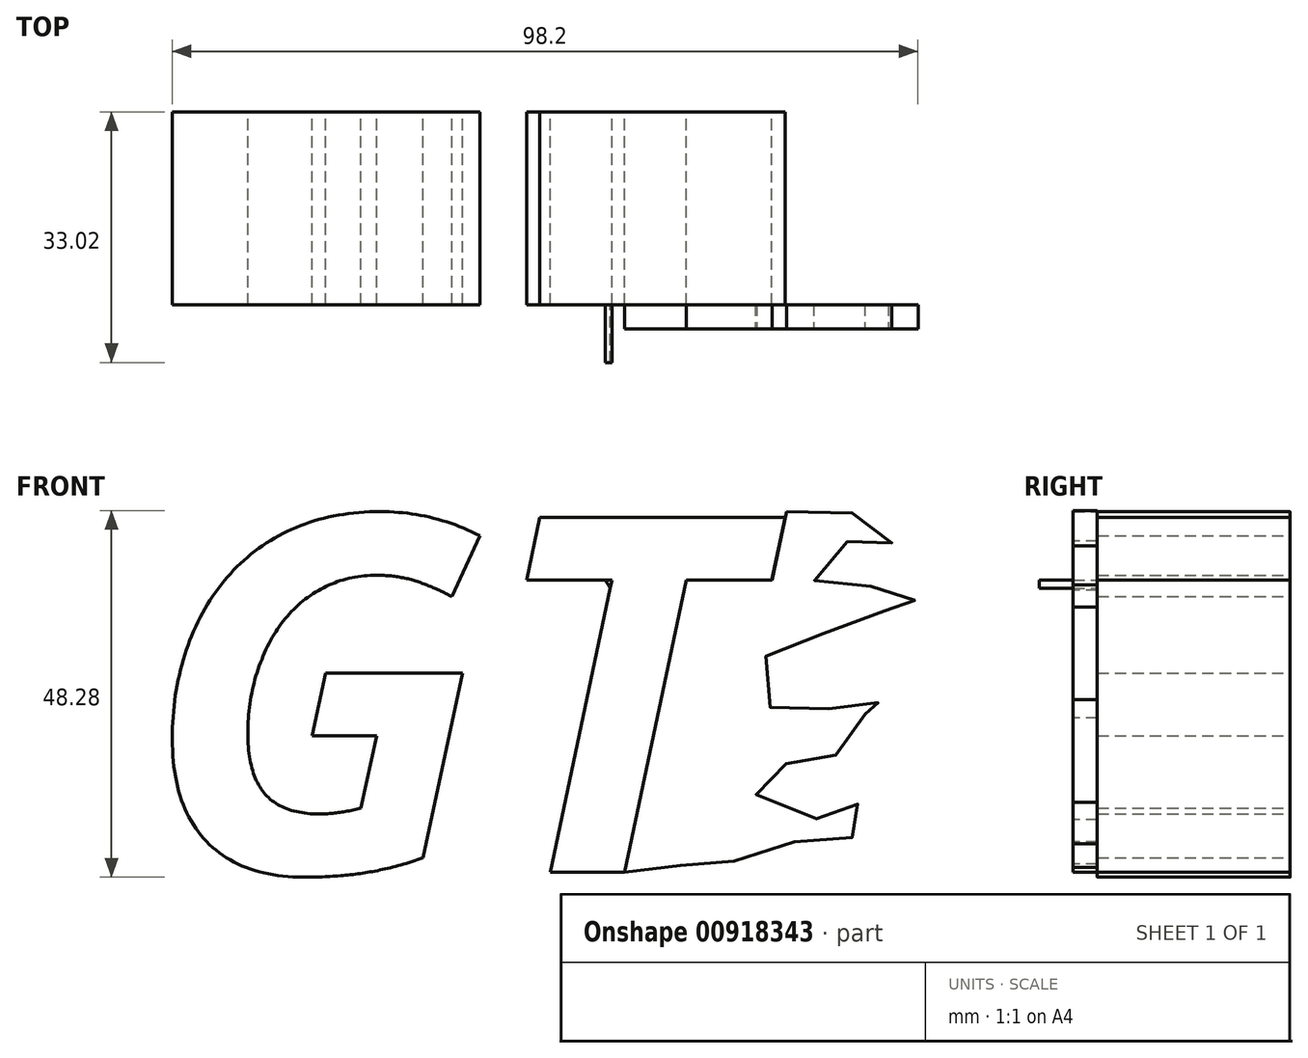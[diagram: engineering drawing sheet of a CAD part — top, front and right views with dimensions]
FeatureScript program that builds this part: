
annotation { "Feature Type Name" : "Feature", "Feature Type Description" : "" }
export const myFeature = defineFeature(function(context is Context, id is Id, definition is map)
    precondition{}
    {
        {
            var Q0;
            Q0=qCreatedBy(makeId("Front.planeOp"),FACE);
            var sketch = newSketch(context, id + "F0", { "sketchPlane" : qUnion([Q0])});
            skText(sketch, "E0", { "text": "GT", "fontName": "NotoSans-BoldItalic.ttf"});
            const initialGuessF0  = {"E0": [-0.04445, -0.02032, 1, 0, 0.04717]};
            skSetInitialGuess(sketch, initialGuessF0);
            skSolve(sketch);
        }
        {
            var Q0;
            Q0 = qSketchRegion(id + "F0", true);
            extrude(context, id + "F1", {"entities" : qUnion([Q0]), "depth" : 25.4 * mm, "offsetDistance" : 25.4 * mm});
        }
        {
            var Q0;
            Q0=makeQuery(id+"F1.opExtrude","CAP_FACE",FACE,{"disambiguationData":[OSD([sQuery(id+"F0.wireOp",EDGE,"E0.sketch_text.stroke-0"),sQuery(id+"F0.wireOp",EDGE,"E0.sketch_text.stroke-1"),sQuery(id+"F0.wireOp",EDGE,"E0.sketch_text.stroke-2"),sQuery(id+"F0.wireOp",EDGE,"E0.sketch_text.stroke-3"),sQuery(id+"F0.wireOp",EDGE,"E0.sketch_text.stroke-4"),sQuery(id+"F0.wireOp",EDGE,"E0.sketch_text.stroke-5"),sQuery(id+"F0.wireOp",EDGE,"E0.sketch_text.stroke-6"),sQuery(id+"F0.wireOp",EDGE,"E0.sketch_text.stroke-7"),sQuery(id+"F0.wireOp",EDGE,"E0.sketch_text.stroke-8"),sQuery(id+"F0.wireOp",EDGE,"E0.sketch_text.stroke-9"),sQuery(id+"F0.wireOp",EDGE,"E0.sketch_text.stroke-10"),sQuery(id+"F0.wireOp",EDGE,"E0.sketch_text.stroke-11"),sQuery(id+"F0.wireOp",EDGE,"E0.sketch_text.stroke-12"),sQuery(id+"F0.wireOp",EDGE,"E0.sketch_text.stroke-13"),sQuery(id+"F0.wireOp",EDGE,"E0.sketch_text.stroke-14"),sQuery(id+"F0.wireOp",EDGE,"E0.sketch_text.stroke-15"),sQuery(id+"F0.wireOp",EDGE,"E0.sketch_text.stroke-16"),sQuery(id+"F0.wireOp",EDGE,"E0.sketch_text.stroke-17"),sQuery(id+"F0.wireOp",EDGE,"E0.sketch_text.stroke-18"),sQuery(id+"F0.wireOp",EDGE,"E0.sketch_text.stroke-19"),sQuery(id+"F0.wireOp",EDGE,"E0.sketch_text.stroke-20"),sQuery(id+"F0.wireOp",EDGE,"E0.sketch_text.stroke-21")])],"isStart":false});
            cPlane(context, id + "F2", {"entities" : qUnion([Q0]), "cplaneType" : CPlaneType.OFFSET, "offset" : 0 * mm, "width" : 152.4 * mm, "height" : 152.4 * mm});
        }
        {
            var Q0;
            Q0=qCreatedBy(id+"F2.planeOp",FACE);
            var sketch = newSketch(context, id + "F3", { "sketchPlane" : qUnion([Q0])});
            skFitSpline(sketch, "E1.0", {"points": [v(-37.14, 12.66) * mm, v(-33.76, 19.57) * mm, v(-27.59, 23.38) * mm]});
            skFitSpline(sketch, "E1.1", {"points": [v(-27.59, 23.38) * mm, v(-21.42, 27.19) * mm, v(-13.13, 27.19) * mm]});
            skFitSpline(sketch, "E1.6", {"points": [v(-13.57, 18.8) * mm, v(-18.47, 18.8) * mm, v(-22.33, 16.15) * mm]});
            skFitSpline(sketch, "E1.7", {"points": [v(-22.33, 16.15) * mm, v(-26.19, 13.5) * mm, v(-28.38, 8.58) * mm]});
            skFitSpline(sketch, "E1.8", {"points": [v(-28.38, 8.58) * mm, v(-30.57, 3.67) * mm, v(-30.57, -1.99) * mm]});
            skFitSpline(sketch, "E1.9", {"points": [v(-30.57, -1.99) * mm, v(-30.57, -7.5) * mm, v(-28.25, -10.07) * mm]});
            skFitSpline(sketch, "E1.10", {"points": [v(-28.25, -10.07) * mm, v(-25.93, -12.65) * mm, v(-21.13, -12.65) * mm]});
            skFitSpline(sketch, "E1.11", {"points": [v(-21.13, -12.65) * mm, v(-18.7, -12.65) * mm, v(-15.7, -11.88) * mm]});
            skLineSegment(sketch, "E1.12", {"start": v(-15.16, -9.47) * mm, "end": v(-13.57, -2.32) * mm});
            skLineSegment(sketch, "E1.13", {"start": v(-13.57, -2.32) * mm, "end": v(-22.12, -2.32) * mm});
            skLineSegment(sketch, "E1.14", {"start": v(-22.12, -2.32) * mm, "end": v(-20.33, 5.95) * mm});
            skLineSegment(sketch, "E1.15", {"start": v(-20.33, 5.95) * mm, "end": v(-2.31, 5.95) * mm});
            skLineSegment(sketch, "E1.16", {"start": v(-2.31, 5.95) * mm, "end": v(-6.89, -15.53) * mm});
            skFitSpline(sketch, "E1.17", {"points": [v(-7.5, -18.44) * mm, v(-11.78, -19.9) * mm, v(-15.45, -20.44) * mm]});
            skFitSpline(sketch, "E1.18", {"points": [v(-15.45, -20.44) * mm, v(-19.11, -20.97) * mm, v(-23.2, -20.97) * mm]});
            skFitSpline(sketch, "E1.19", {"points": [v(-23.2, -20.97) * mm, v(-31.49, -20.97) * mm, v(-36, -16.26) * mm]});
            skFitSpline(sketch, "E1.20", {"points": [v(-36, -16.26) * mm, v(-40.52, -11.56) * mm, v(-40.52, -2.76) * mm]});
            skFitSpline(sketch, "E1.21", {"points": [v(-40.52, -2.76) * mm, v(-40.52, 5.75) * mm, v(-37.14, 12.66) * mm]});
            skLineSegment(sketch, "E2.2", {"start": v(40.2, 26.45) * mm, "end": v(38.44, 18.2) * mm});
            skLineSegment(sketch, "E2.3", {"start": v(38.44, 18.2) * mm, "end": v(27.15, 18.2) * mm});
            skLineSegment(sketch, "E2.4", {"start": v(27.15, 18.2) * mm, "end": v(19.02, -20.32) * mm});
            skLineSegment(sketch, "E2.5", {"start": v(19.02, -20.32) * mm, "end": v(9.26, -20.32) * mm});
            skLineSegment(sketch, "E2.6", {"start": v(9.26, -20.32) * mm, "end": v(17.4, 18.2) * mm});
            skLineSegment(sketch, "E2.7", {"start": v(17.4, 18.2) * mm, "end": v(6.13, 18.2) * mm});
            skLineSegment(sketch, "E3", {"start": v(-13.13, 27.19) * mm, "end": v(40.36, 27.19) * mm});
            skLineSegment(sketch, "E4", {"start": v(6.13, 18.2) * mm, "end": v(-16.98, 18.2) * mm});
            skPoint(sketch, "E5.orphan", {"position": v(-3.7, 15.99) * mm});
            skPoint(sketch, "E6.orphan", {"position": v(-8.43, 18.04) * mm});
            skPoint(sketch, "E7.orphan", {"position": v(-13.57, 18.8) * mm});
            skPoint(sketch, "E1.2.end.orphan", {"position": v(-0.01, 24.01) * mm});
            skPoint(sketch, "E2.1.start.orphan", {"position": v(7.9, 26.45) * mm});
            skLineSegment(sketch, "E8", {"start": v(40.2, 26.45) * mm, "end": v(40.36, 27.19) * mm});
            skPoint(sketch, "E9.visualSharp", {"position": v(-18, 18.2) * mm});
            skArc(sketch, "E9.filletArc", {"start": v(-16.98, 18.2) * mm, "mid": v(-18.16, 18.09) * mm, "end": v(-19.3, 17.76) * mm});
            skPoint(sketch, "E10.visualSharp", {"position": v(-15.7, -11.88) * mm});
            skArc(sketch, "E10.filletArc", {"start": v(-18.3, -12.42) * mm, "mid": v(-16.28, -11.43) * mm, "end": v(-15.16, -9.47) * mm});
            skPoint(sketch, "E11.visualSharp", {"position": v(-7.5, -18.44) * mm});
            skArc(sketch, "E11.filletArc", {"start": v(-10.5, -19.37) * mm, "mid": v(-8.15, -17.95) * mm, "end": v(-6.89, -15.53) * mm});
            skArc(sketch, "E12", {"start": v(-14.72, 33.34) * mm, "mid": v(-45.06, -1.74) * mm, "end": v(-11.23, -33.48) * mm, "construction": true});
            skFitSpline(sketch, "E13", {"points": [v(-14.72, 33.34) * mm, v(37.18, 33.37) * mm, v(58.87, 35.5) * mm, v(76.74, 32.31) * mm, v(64.4, 31.46) * mm, v(56.96, 24.65) * mm, v(67.5, 20.64) * mm, v(87.92, 28.3) * mm, v(67.08, 12.56) * mm, v(53.46, 11.07) * mm, v(61.33, 0) * mm, v(87.92, 10.86) * mm, v(69.63, -7.22) * mm, v(52.19, -9.99) * mm, v(62.82, -20.2) * mm, v(80.48, -9.35) * mm, v(64.31, -28.07) * mm, v(-11.23, -33.48) * mm], "startDerivative": vector(608.28, -20.2) * mm, "endDerivative": vector(-707.93, -8.2) * mm, "construction": true});
            skArc(sketch, "E14.trimOffspring", {"start": v(17.16, 17.1) * mm, "mid": v(16.83, 17.66) * mm, "end": v(16.49, 18.2) * mm});
            skFitSpline(sketch, "E15", {"points": [v(40.36, 27.19) * mm, v(47.88, 27.19) * mm, v(52.24, 25.58) * mm, v(54.2, 22.87) * mm, v(50.74, 23.17) * mm, v(46.83, 22.57) * mm, v(43.97, 18.36) * mm, v(47.28, 16.86) * mm, v(54.2, 17.46) * mm, v(56.76, 15.95) * mm, v(57.66, 14.75) * mm, v(54.65, 14.6) * mm, v(50.14, 12.35) * mm, v(41.42, 10.4) * mm, v(37.35, 7.68) * mm, v(36.9, 2.87) * mm, v(42.62, 0) * mm, v(47.28, 1.97) * mm, v(51.34, 2.27) * mm, v(53.75, 1.52) * mm, v(51.8, 1.22) * mm, v(49.69, -1.2) * mm, v(46.98, -4.8) * mm, v(43.07, -5.55) * mm, v(38.86, -6.6) * mm, v(36.3, -9.16) * mm, v(37.8, -11.57) * mm, v(46.38, -13.37) * mm, v(48.63, -12.47) * mm, v(50.29, -11.12) * mm, v(50.29, -14.27) * mm, v(46.53, -16.53) * mm, v(40.36, -16.38) * mm, v(34.05, -18.64) * mm, v(28.63, -19.69) * mm, v(24.72, -19.24) * mm, v(19.02, -20.32) * mm], "startDerivative": vector(219.9, 9.12) * mm, "endDerivative": vector(-187.1, -51) * mm});
            skSolve(sketch);
        }
        {
            var Q0;
            {var subQ3=sQuery(id+"F3.wireOp",EDGE,"E14.trimOffspring");Q0=makeQuery(id+"F3.imprint","IMPRINT",FACE,{"disambiguationData":[TD([[makeQuery(id+"F3.imprint","IMPRINT",EDGE,{"derivedFrom":subQ3}),-1.0]])]});}
            var Q1;
            Q1=makeQuery(id+"F3.imprint","IMPRINT",FACE,{"disambiguationData":[TD([[makeQuery(id+"F3.imprint","IMPRINT",EDGE,{"derivedFrom":sQuery(id+"F3.wireOp",EDGE,"E1.0")}),-1.0]])]});
            extrude(context, id + "F4", {"entities" : qUnion([Q0, Q1]), "depth" : 7.62 * mm, "offsetDistance" : 25.4 * mm});
        }
        {
            var Q0;
            Q0 = qSketchRegion(id + "F3", true);
            extrude(context, id + "F5", {"entities" : qUnion([Q0]), "operationType" : NewBodyOperationType.ADD, "depth" : 3.17 * mm, "offsetDistance" : 25.4 * mm});
        }
    });
